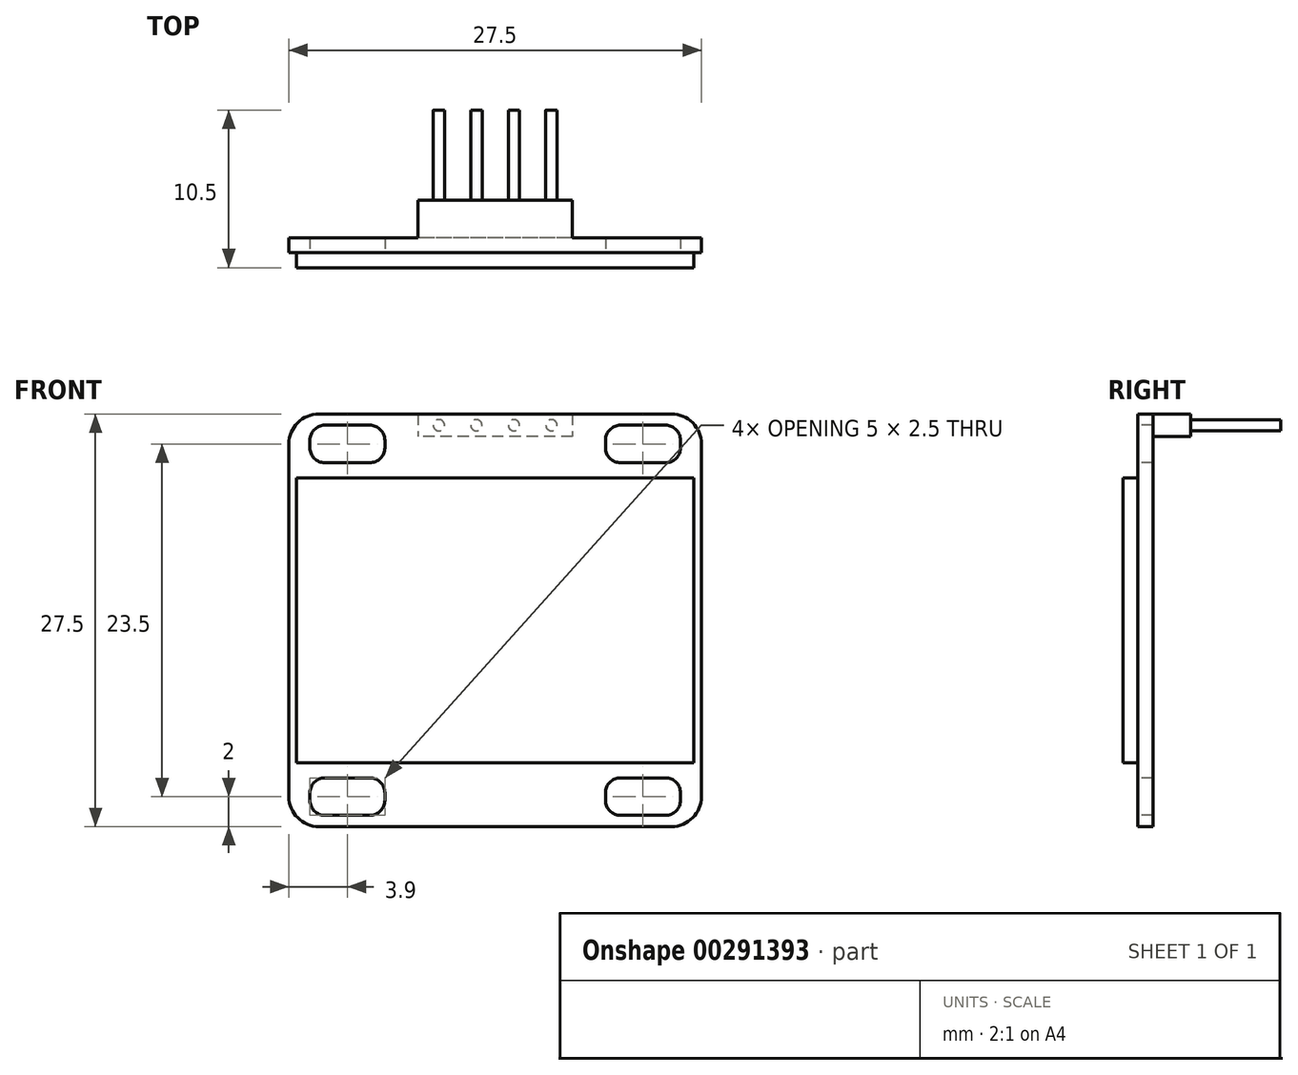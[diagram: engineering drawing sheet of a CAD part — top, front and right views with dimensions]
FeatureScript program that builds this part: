
annotation { "Feature Type Name" : "Feature", "Feature Type Description" : "" }
export const myFeature = defineFeature(function(context is Context, id is Id, definition is map)
    precondition{}
    {
        {
            var Q0;
            Q0=qCreatedBy(makeId("Front.planeOp"),FACE);
            var sketch = newSketch(context, id + "F0", { "sketchPlane" : qUnion([Q0])});
            skLineSegment(sketch, "E0.bottom", {"start": v(11.75, 13.75) * mm, "end": v(-11.75, 13.75) * mm});
            skLineSegment(sketch, "E0.top", {"start": v(11.75, -13.75) * mm, "end": v(-11.75, -13.75) * mm});
            skLineSegment(sketch, "E0.left", {"start": v(13.75, 11.75) * mm, "end": v(13.75, -11.75) * mm});
            skLineSegment(sketch, "E0.right", {"start": v(-13.75, 11.75) * mm, "end": v(-13.75, -11.75) * mm});
            skPoint(sketch, "E0.middle", {"position": v(0, 0) * mm});
            skPoint(sketch, "E1.visualSharp", {"position": v(-13.75, 13.75) * mm});
            skArc(sketch, "E1.filletArc", {"start": v(-11.75, 13.75) * mm, "mid": v(-13.16, 13.16) * mm, "end": v(-13.75, 11.75) * mm});
            skPoint(sketch, "E2.visualSharp", {"position": v(13.75, 13.75) * mm});
            skArc(sketch, "E2.filletArc", {"start": v(13.75, 11.75) * mm, "mid": v(13.16, 13.16) * mm, "end": v(11.75, 13.75) * mm});
            skPoint(sketch, "E3.visualSharp", {"position": v(13.75, -13.75) * mm});
            skArc(sketch, "E3.filletArc", {"start": v(11.75, -13.75) * mm, "mid": v(13.16, -13.16) * mm, "end": v(13.75, -11.75) * mm});
            skPoint(sketch, "E4.visualSharp", {"position": v(-13.75, -13.75) * mm});
            skArc(sketch, "E4.filletArc", {"start": v(-13.75, -11.75) * mm, "mid": v(-13.16, -13.16) * mm, "end": v(-11.75, -13.75) * mm});
            skLineSegment(sketch, "E5.bottom", {"start": v(8.35, 10.5) * mm, "end": v(11.35, 10.5) * mm});
            skLineSegment(sketch, "E5.top", {"start": v(8.35, 13) * mm, "end": v(11.35, 13) * mm});
            skLineSegment(sketch, "E5.left", {"start": v(7.35, 11.5) * mm, "end": v(7.35, 12) * mm});
            skLineSegment(sketch, "E5.right", {"start": v(12.35, 11.5) * mm, "end": v(12.35, 12) * mm});
            skLineSegment(sketch, "E6", {"start": v(0, 13.75) * mm, "end": v(0, -13.75) * mm, "construction": true});
            skLineSegment(sketch, "E7", {"start": v(-13.75, 0) * mm, "end": v(13.75, 0) * mm, "construction": true});
            skLineSegment(sketch, "E8.MirrorCS", {"start": v(-7.35, 11.5) * mm, "end": v(-7.35, 12) * mm});
            skLineSegment(sketch, "E9.MirrorCS", {"start": v(-8.35, 13) * mm, "end": v(-11.35, 13) * mm});
            skLineSegment(sketch, "E10.MirrorCS", {"start": v(-12.35, 11.5) * mm, "end": v(-12.35, 12) * mm});
            skLineSegment(sketch, "E11.MirrorCS", {"start": v(-8.35, 10.5) * mm, "end": v(-11.35, 10.5) * mm});
            skLineSegment(sketch, "E12.MirrorCS", {"start": v(-8.35, -10.5) * mm, "end": v(-11.35, -10.5) * mm});
            skLineSegment(sketch, "E13.MirrorCS", {"start": v(-12.35, -11.5) * mm, "end": v(-12.35, -12) * mm});
            skLineSegment(sketch, "E14.MirrorCS", {"start": v(-8.35, -13) * mm, "end": v(-11.35, -13) * mm});
            skLineSegment(sketch, "E15.MirrorCS", {"start": v(-7.35, -11.5) * mm, "end": v(-7.35, -12) * mm});
            skLineSegment(sketch, "E16.MirrorCS", {"start": v(7.35, -11.5) * mm, "end": v(7.35, -12) * mm});
            skLineSegment(sketch, "E17.MirrorCS", {"start": v(8.35, -13) * mm, "end": v(11.35, -13) * mm});
            skLineSegment(sketch, "E18.MirrorCS", {"start": v(12.35, -11.5) * mm, "end": v(12.35, -12) * mm});
            skLineSegment(sketch, "E19.MirrorCS", {"start": v(8.35, -10.5) * mm, "end": v(11.35, -10.5) * mm});
            skPoint(sketch, "E20.visualSharp", {"position": v(7.35, 13) * mm});
            skArc(sketch, "E20.filletArc", {"start": v(8.35, 13) * mm, "mid": v(7.64, 12.7) * mm, "end": v(7.35, 12) * mm});
            skPoint(sketch, "E21.visualSharp", {"position": v(12.35, 13) * mm});
            skArc(sketch, "E21.filletArc", {"start": v(12.35, 12) * mm, "mid": v(12.06, 12.7) * mm, "end": v(11.35, 13) * mm});
            skPoint(sketch, "E22.visualSharp", {"position": v(12.35, 10.5) * mm});
            skArc(sketch, "E22.filletArc", {"start": v(11.35, 10.5) * mm, "mid": v(12.06, 10.8) * mm, "end": v(12.35, 11.5) * mm});
            skPoint(sketch, "E23.visualSharp", {"position": v(7.35, 10.5) * mm});
            skArc(sketch, "E23.filletArc", {"start": v(7.35, 11.5) * mm, "mid": v(7.64, 10.8) * mm, "end": v(8.35, 10.5) * mm});
            skPoint(sketch, "E24.visualSharp", {"position": v(-7.35, 13) * mm});
            skArc(sketch, "E24.filletArc", {"start": v(-7.35, 12) * mm, "mid": v(-7.64, 12.7) * mm, "end": v(-8.35, 13) * mm});
            skPoint(sketch, "E25.visualSharp", {"position": v(-7.35, 10.5) * mm});
            skArc(sketch, "E25.filletArc", {"start": v(-8.35, 10.5) * mm, "mid": v(-7.64, 10.8) * mm, "end": v(-7.35, 11.5) * mm});
            skPoint(sketch, "E26.visualSharp", {"position": v(-12.35, 10.5) * mm});
            skArc(sketch, "E26.filletArc", {"start": v(-12.35, 11.5) * mm, "mid": v(-12.06, 10.8) * mm, "end": v(-11.35, 10.5) * mm});
            skPoint(sketch, "E27.visualSharp", {"position": v(-12.35, 13) * mm});
            skArc(sketch, "E27.filletArc", {"start": v(-11.35, 13) * mm, "mid": v(-12.06, 12.7) * mm, "end": v(-12.35, 12) * mm});
            skPoint(sketch, "E28.visualSharp", {"position": v(-12.35, -10.5) * mm});
            skArc(sketch, "E28.filletArc", {"start": v(-11.35, -10.5) * mm, "mid": v(-12.06, -10.8) * mm, "end": v(-12.35, -11.5) * mm});
            skPoint(sketch, "E29.visualSharp", {"position": v(-7.35, -10.5) * mm});
            skArc(sketch, "E29.filletArc", {"start": v(-7.35, -11.5) * mm, "mid": v(-7.64, -10.8) * mm, "end": v(-8.35, -10.5) * mm});
            skPoint(sketch, "E30.visualSharp", {"position": v(-7.35, -13) * mm});
            skArc(sketch, "E30.filletArc", {"start": v(-8.35, -13) * mm, "mid": v(-7.64, -12.7) * mm, "end": v(-7.35, -12) * mm});
            skPoint(sketch, "E31.visualSharp", {"position": v(-12.35, -13) * mm});
            skArc(sketch, "E31.filletArc", {"start": v(-12.35, -12) * mm, "mid": v(-12.06, -12.7) * mm, "end": v(-11.35, -13) * mm});
            skPoint(sketch, "E32.visualSharp", {"position": v(7.35, -10.5) * mm});
            skArc(sketch, "E32.filletArc", {"start": v(8.35, -10.5) * mm, "mid": v(7.64, -10.8) * mm, "end": v(7.35, -11.5) * mm});
            skPoint(sketch, "E33.visualSharp", {"position": v(12.35, -10.5) * mm});
            skArc(sketch, "E33.filletArc", {"start": v(12.35, -11.5) * mm, "mid": v(12.06, -10.8) * mm, "end": v(11.35, -10.5) * mm});
            skPoint(sketch, "E34.visualSharp", {"position": v(12.35, -13) * mm});
            skArc(sketch, "E34.filletArc", {"start": v(11.35, -13) * mm, "mid": v(12.06, -12.7) * mm, "end": v(12.35, -12) * mm});
            skPoint(sketch, "E35.visualSharp", {"position": v(7.35, -13) * mm});
            skArc(sketch, "E35.filletArc", {"start": v(7.35, -12) * mm, "mid": v(7.64, -12.7) * mm, "end": v(8.35, -13) * mm});
            skLineSegment(sketch, "E36", {"start": v(7.35, 11.75) * mm, "end": v(12.35, 11.75) * mm, "construction": true});
            skSolve(sketch);
        }
        {
            var Q0;
            Q0 = qSketchRegion(id + "F0", true);
            extrude(context, id + "F1", {"entities" : qUnion([Q0]), "oppositeDirection" : true, "depth" : 1 * mm});
        }
        {
            var Q0;
            Q0=makeQuery(id+"F1.opExtrude","CAP_FACE",FACE,{"disambiguationData":[OSD([sQuery(id+"F0.wireOp",EDGE,"E0.bottom"),sQuery(id+"F0.wireOp",EDGE,"E0.top"),sQuery(id+"F0.wireOp",EDGE,"E0.left"),sQuery(id+"F0.wireOp",EDGE,"E0.right"),sQuery(id+"F0.wireOp",EDGE,"E1.filletArc"),sQuery(id+"F0.wireOp",EDGE,"E2.filletArc"),sQuery(id+"F0.wireOp",EDGE,"E3.filletArc"),sQuery(id+"F0.wireOp",EDGE,"E4.filletArc"),sQuery(id+"F0.wireOp",EDGE,"E5.bottom"),sQuery(id+"F0.wireOp",EDGE,"E5.top"),sQuery(id+"F0.wireOp",EDGE,"E5.left"),sQuery(id+"F0.wireOp",EDGE,"E5.right"),sQuery(id+"F0.wireOp",EDGE,"E8.MirrorCS"),sQuery(id+"F0.wireOp",EDGE,"E9.MirrorCS"),sQuery(id+"F0.wireOp",EDGE,"E10.MirrorCS"),sQuery(id+"F0.wireOp",EDGE,"E11.MirrorCS"),sQuery(id+"F0.wireOp",EDGE,"E12.MirrorCS"),sQuery(id+"F0.wireOp",EDGE,"E13.MirrorCS"),sQuery(id+"F0.wireOp",EDGE,"E14.MirrorCS"),sQuery(id+"F0.wireOp",EDGE,"E15.MirrorCS"),sQuery(id+"F0.wireOp",EDGE,"E16.MirrorCS"),sQuery(id+"F0.wireOp",EDGE,"E17.MirrorCS"),sQuery(id+"F0.wireOp",EDGE,"E18.MirrorCS"),sQuery(id+"F0.wireOp",EDGE,"E19.MirrorCS"),sQuery(id+"F0.wireOp",EDGE,"E20.filletArc"),sQuery(id+"F0.wireOp",EDGE,"E21.filletArc"),sQuery(id+"F0.wireOp",EDGE,"E22.filletArc"),sQuery(id+"F0.wireOp",EDGE,"E23.filletArc"),sQuery(id+"F0.wireOp",EDGE,"E24.filletArc"),sQuery(id+"F0.wireOp",EDGE,"E25.filletArc"),sQuery(id+"F0.wireOp",EDGE,"E26.filletArc"),sQuery(id+"F0.wireOp",EDGE,"E27.filletArc"),sQuery(id+"F0.wireOp",EDGE,"E28.filletArc"),sQuery(id+"F0.wireOp",EDGE,"E29.filletArc"),sQuery(id+"F0.wireOp",EDGE,"E30.filletArc"),sQuery(id+"F0.wireOp",EDGE,"E31.filletArc"),sQuery(id+"F0.wireOp",EDGE,"E32.filletArc"),sQuery(id+"F0.wireOp",EDGE,"E33.filletArc"),sQuery(id+"F0.wireOp",EDGE,"E34.filletArc"),sQuery(id+"F0.wireOp",EDGE,"E35.filletArc")])],"isStart":true});
            var sketch = newSketch(context, id + "F2", { "sketchPlane" : qUnion([Q0])});
            skLineSegment(sketch, "E37.bottom", {"start": v(-13.25, 9.5) * mm, "end": v(13.25, 9.5) * mm});
            skLineSegment(sketch, "E37.top", {"start": v(-13.25, -9.5) * mm, "end": v(13.25, -9.5) * mm});
            skLineSegment(sketch, "E37.left", {"start": v(-13.25, 9.5) * mm, "end": v(-13.25, -9.5) * mm});
            skLineSegment(sketch, "E37.right", {"start": v(13.25, 9.5) * mm, "end": v(13.25, -9.5) * mm});
            skPoint(sketch, "E37.middle", {"position": v(0, 0) * mm});
            skSolve(sketch);
        }
        {
            var Q0;
            Q0 = qSketchRegion(id + "F2", true);
            extrude(context, id + "F3", {"entities" : qUnion([Q0]), "operationType" : NewBodyOperationType.ADD, "depth" : 1 * mm});
        }
        {
            var Q0;
            Q0=makeQuery(id+"F1.opExtrude","CAP_FACE",FACE,{"disambiguationData":[OSD([sQuery(id+"F0.wireOp",EDGE,"E0.bottom"),sQuery(id+"F0.wireOp",EDGE,"E0.top"),sQuery(id+"F0.wireOp",EDGE,"E0.left"),sQuery(id+"F0.wireOp",EDGE,"E0.right"),sQuery(id+"F0.wireOp",EDGE,"E1.filletArc"),sQuery(id+"F0.wireOp",EDGE,"E2.filletArc"),sQuery(id+"F0.wireOp",EDGE,"E3.filletArc"),sQuery(id+"F0.wireOp",EDGE,"E4.filletArc"),sQuery(id+"F0.wireOp",EDGE,"E5.bottom"),sQuery(id+"F0.wireOp",EDGE,"E5.top"),sQuery(id+"F0.wireOp",EDGE,"E5.left"),sQuery(id+"F0.wireOp",EDGE,"E5.right"),sQuery(id+"F0.wireOp",EDGE,"E8.MirrorCS"),sQuery(id+"F0.wireOp",EDGE,"E9.MirrorCS"),sQuery(id+"F0.wireOp",EDGE,"E10.MirrorCS"),sQuery(id+"F0.wireOp",EDGE,"E11.MirrorCS"),sQuery(id+"F0.wireOp",EDGE,"E12.MirrorCS"),sQuery(id+"F0.wireOp",EDGE,"E13.MirrorCS"),sQuery(id+"F0.wireOp",EDGE,"E14.MirrorCS"),sQuery(id+"F0.wireOp",EDGE,"E15.MirrorCS"),sQuery(id+"F0.wireOp",EDGE,"E16.MirrorCS"),sQuery(id+"F0.wireOp",EDGE,"E17.MirrorCS"),sQuery(id+"F0.wireOp",EDGE,"E18.MirrorCS"),sQuery(id+"F0.wireOp",EDGE,"E19.MirrorCS"),sQuery(id+"F0.wireOp",EDGE,"E20.filletArc"),sQuery(id+"F0.wireOp",EDGE,"E21.filletArc"),sQuery(id+"F0.wireOp",EDGE,"E22.filletArc"),sQuery(id+"F0.wireOp",EDGE,"E23.filletArc"),sQuery(id+"F0.wireOp",EDGE,"E24.filletArc"),sQuery(id+"F0.wireOp",EDGE,"E25.filletArc"),sQuery(id+"F0.wireOp",EDGE,"E26.filletArc"),sQuery(id+"F0.wireOp",EDGE,"E27.filletArc"),sQuery(id+"F0.wireOp",EDGE,"E28.filletArc"),sQuery(id+"F0.wireOp",EDGE,"E29.filletArc"),sQuery(id+"F0.wireOp",EDGE,"E30.filletArc"),sQuery(id+"F0.wireOp",EDGE,"E31.filletArc"),sQuery(id+"F0.wireOp",EDGE,"E32.filletArc"),sQuery(id+"F0.wireOp",EDGE,"E33.filletArc"),sQuery(id+"F0.wireOp",EDGE,"E34.filletArc"),sQuery(id+"F0.wireOp",EDGE,"E35.filletArc")])],"isStart":false});
            var sketch = newSketch(context, id + "F4", { "sketchPlane" : qUnion([Q0])});
            skLineSegment(sketch, "E38.bottom", {"start": v(-5.15, 13.75) * mm, "end": v(5.15, 13.75) * mm});
            skLineSegment(sketch, "E38.top", {"start": v(-5.15, 12.25) * mm, "end": v(5.15, 12.25) * mm});
            skLineSegment(sketch, "E38.left", {"start": v(-5.15, 13.75) * mm, "end": v(-5.15, 12.25) * mm});
            skLineSegment(sketch, "E38.right", {"start": v(5.15, 13.75) * mm, "end": v(5.15, 12.25) * mm});
            skPoint(sketch, "E38.middle", {"position": v(0, 13) * mm});
            skSolve(sketch);
        }
        {
            var Q0;
            Q0 = qSketchRegion(id + "F4", true);
            extrude(context, id + "F5", {"entities" : qUnion([Q0]), "operationType" : NewBodyOperationType.ADD, "depth" : 2.5 * mm});
        }
        {
            var Q0;
            Q0=makeQuery(id+"F5.opExtrude","CAP_FACE",FACE,{"disambiguationData":[OSD([sQuery(id+"F4.wireOp",EDGE,"E38.bottom"),sQuery(id+"F4.wireOp",EDGE,"E38.top"),sQuery(id+"F4.wireOp",EDGE,"E38.left"),sQuery(id+"F4.wireOp",EDGE,"E38.right")])],"isStart":false});
            var sketch = newSketch(context, id + "F6", { "sketchPlane" : qUnion([Q0])});
            skLineSegment(sketch, "E39", {"start": v(0, 13.75) * mm, "end": v(0, 12.25) * mm, "construction": true});
            skLineSegment(sketch, "E40", {"start": v(-5.15, 13) * mm, "end": v(5.15, 13) * mm, "construction": true});
            skCircle(sketch, "E41", {"center": v(-1.25, 13) * mm, "radius": 0.38 * mm});
            skCircle(sketch, "E42.1.0.0", {"center": v(-3.75, 13) * mm, "radius": 0.38 * mm});
            skLineSegment(sketch, "E42.direction1", {"start": v(-1.25, 13) * mm, "end": v(-3.75, 13) * mm, "construction": true});
            skCircle(sketch, "E43.MirrorC", {"center": v(1.25, 13) * mm, "radius": 0.38 * mm});
            skCircle(sketch, "E44.MirrorC", {"center": v(3.75, 13) * mm, "radius": 0.38 * mm});
            skSolve(sketch);
        }
        {
            var Q0;
            Q0 = qSketchRegion(id + "F6", true);
            extrude(context, id + "F7", {"entities" : qUnion([Q0]), "operationType" : NewBodyOperationType.ADD, "depth" : 6 * mm});
        }
    });
